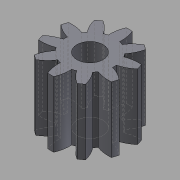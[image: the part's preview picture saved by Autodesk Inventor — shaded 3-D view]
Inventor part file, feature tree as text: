
AUTODESK INVENTOR PART (.ipt)
format: ipt  version: 2015 (Build 190159000, 159)  size: 168,960 bytes
history: native  units: in
note: dims shown in document units (in); Inventor stores cm internally (conversion verified against a paired STEP export)
features: other x13, sketch x3, plane x2
ambient origin geometry x8: Origin, YZ Plane, XZ Plane, XY Plane, X Axis, Y Axis, Z Axis, Center Point
bodies: Solid1 (feature_tree)
feature tree (18):
  other  "Spur Gear1"
  other  "Solid1::Spur Gear1"
  other  "TaggingFeature1"
  sketch  "Sketch1"  dims[d0=0.3937in]
  sketch  "Sketch2"  dims[d16=0.4724in d17=0.0in d41=0.0in d43=0.4724in d46=0.4724in d47=0.0in d48=0.0in]
  sketch  "Sketch3"
  plane  "XZ Plane_1"
  plane  "Work Plane2"
  other  "Z Axis_1"
  other  "Srf1"
  other  "Srf1::Derived"
  other  "Distance iMate"
  other  "Align iMate"
  other  "Mesh iMate"
  other  "Axis iMate"
  other  "Position iMate"
  other  "Mesh iMate2"
  other  "Start plane iMate"
